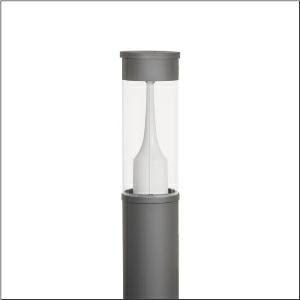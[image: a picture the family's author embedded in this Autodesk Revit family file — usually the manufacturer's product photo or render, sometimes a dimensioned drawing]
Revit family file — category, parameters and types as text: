
# Revit family: city-light_260_iq___p1_0a_5xa5295ff14h_c360
name_source: partatom
category: Lighting Fixtures
units: mm (PartAtom-declared; Revit-internal decimal feet)

## family parameters
Cut with Voids When Loaded = No
Host = Face
Light Source = No
Part Type = Normal
Room Calculation Point = No
Round Connector Dimension = Use Diameter
Shared = No

## types (1)
- --- (1 x LED, 1510 lm, 10.5 W, 3000K)
    Apparent Load = 11 VA
    CIE Flux Codes = 32 61 90 93 100
    Color Rendering = 70
    Color Temperature = 3000K
    Default Elevation = 1800 mm
    Description = City-Light 260 iQ, light pillar, Module 540 iQ-SR, primary light control with 3 zone facetted reflector, of plastic, silver coated, highly specular, structured, primary optical cover: cover, of PMMA, transparent, light distribution: P1.0a, primary light characteristic: strongly asymmetric, LED, High Power LED, rated luminous flux: 1.510lm, luminous efficacy: 144lm/W, light colour: 730, colour temperature: 3000K, control gear: ECG iQ, control: Auto-Match, Temp-Guard, Lumen-Switch, Night-Set, Smart-Wire, Light-Fading, Desk-Remote (wireless, voltage-free reading and setting of iQ features in the workshop via application-optimized NFC function/RFID function), optimised constant luminous flux control (CLO 2.0), Street-Remote, presetting dimming logarithmic, with terminal, 6-pole, max. 2.5mm², mains connection: 230..240V, AC, 50/60Hz, start of lifetime: 11W, end of service life: 11W, reduction: 5W, luminaire housing, cylindrical, of extruded aluminium section, coated, Siteco® metallic grey (DB 702S), length: 2.600mm, diameter: 200mm, Module 540 iQ-SR, traffic white (RAL 9016), equipment: standard, protection rating (complete): IP65, insulation class (complete): insulation class II (safety insulation), certification: CE, ENEC, VDE, packaging unit: 1 piece

Light Distribution: P1.0a
    Height = 500 mm
    Lamp = 1 x LED
    Lamp Light Flux = 1510 lm
    Lamp Power = 10.5 W
    Lamp count = 1
    Length = 200 mm  [stored 0.656168 ft]
    Luminous efficacy = 144 lm/W
    Manufacturer = Siteco
    ModVariant = No
    Model = 5XA5295FF14H
    Mounting Place = Floor
    Mounting Type = Freestanding
    Number of Poles = 1
    OnlyDefault = Yes
    Power Factor = 1
    Product Name = City-Light 260 iQ | P1.0a
    Product group = light pillar
    ProductGroupID = 1303
    Protection Class = Protection class II
    Protection Degree = IP 65
    RLX_Detail_Level = 1
    RLX_Emergency_Light_Flux = 0 lm
    RLX_Emergency_Type = 0
    RLX_Emergency_Type_DB = No
    RlxData = <blob elided: 52629 chars, md5=7ebfc44e>
    Socket = socket
    Standby Power = 0 W
    System Light Flux = 1510 lm
    System Power = 11 W
    Type Comments = factory setting: luminous flux: 100 % | dim-lin: 254 | 419 mA
    Type Image = l_1006918.jpg
    URL = http://relux.com
    VarID = @adj_109673
    Voltage = 0 V
    Weight = 0.00 kg
    Width = 0 mm  [stored 0 ft]

note: [stored X ft] marks values corroborated as IEEE doubles in the binary element streams (Revit-internal decimal feet)

## geometry (parser evidence)
native form markers: Blend x4, Sweep x12
no freeform markers — native parametric forms only
